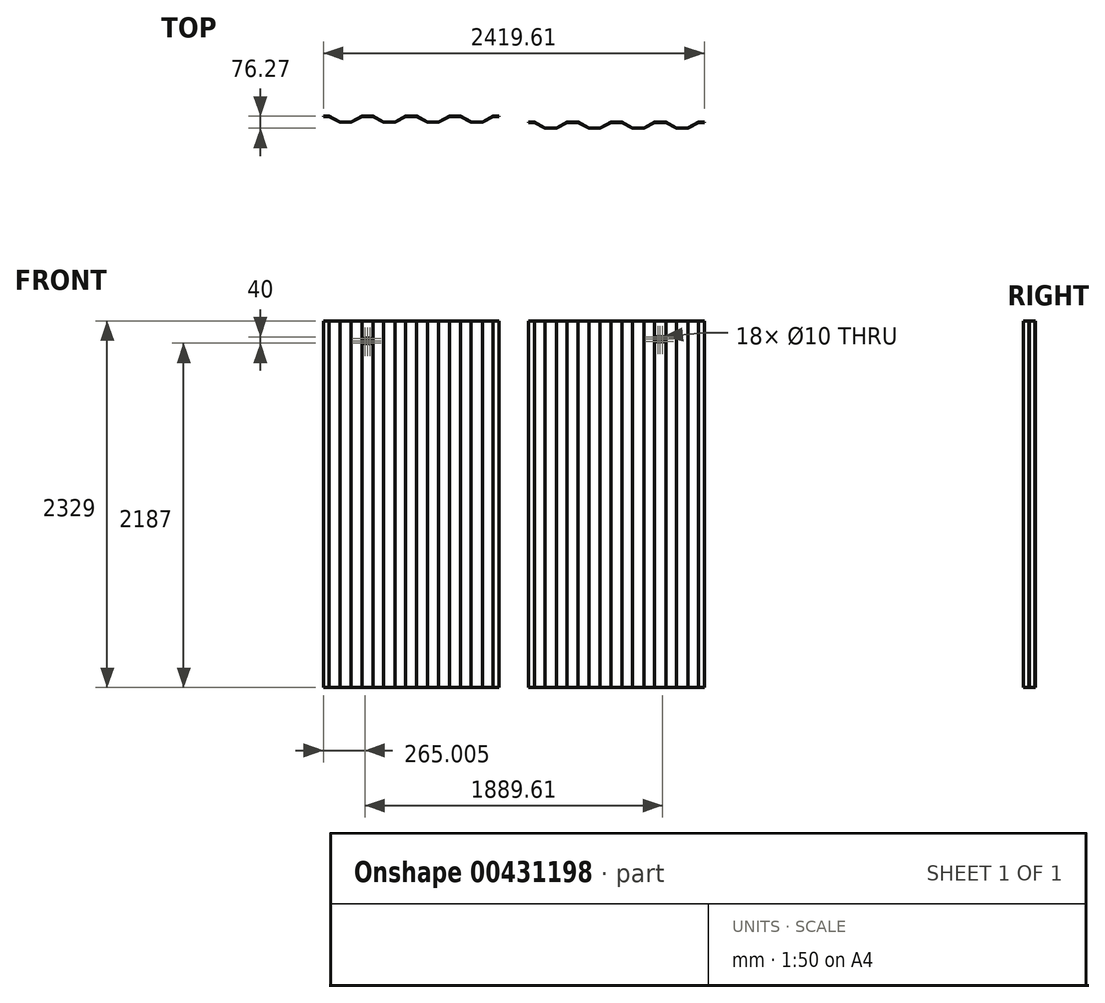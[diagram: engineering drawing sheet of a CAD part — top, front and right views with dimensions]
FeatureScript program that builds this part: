
annotation { "Feature Type Name" : "Feature", "Feature Type Description" : "" }
export const myFeature = defineFeature(function(context is Context, id is Id, definition is map)
    precondition{}
    {
        {
            var Q0;
            Q0=qCreatedBy(makeId("Top.planeOp"),FACE);
            var sketch = newSketch(context, id + "F0", { "sketchPlane" : qUnion([Q0])});
            skPoint(sketch, "E0", {"position": v(0, -36) * mm});
            skPoint(sketch, "E1", {"position": v(37, 0) * mm});
            skPoint(sketch, "E2", {"position": v(37, -36) * mm});
            skPoint(sketch, "E3", {"position": v(105, -36) * mm});
            skPoint(sketch, "E4", {"position": v(177, -36) * mm});
            skPoint(sketch, "E5", {"position": v(245, -36) * mm});
            skPoint(sketch, "E6", {"position": v(315, -36) * mm});
            skLineSegment(sketch, "E7", {"start": v(0, 0) * mm, "end": v(37, 0) * mm});
            skLineSegment(sketch, "E8", {"start": v(37, 0) * mm, "end": v(105, -36) * mm});
            skLineSegment(sketch, "E9", {"start": v(177, -36) * mm, "end": v(105, -36) * mm});
            skLineSegment(sketch, "E10", {"start": v(177, -36) * mm, "end": v(245, 0) * mm});
            skLineSegment(sketch, "E11", {"start": v(245, 0) * mm, "end": v(315, 0) * mm});
            skLineSegment(sketch, "E12.0", {"start": v(0, 2) * mm, "end": v(37.5, 2) * mm});
            skLineSegment(sketch, "E13", {"start": v(0, 0) * mm, "end": v(0, 2) * mm});
            skLineSegment(sketch, "E14.0", {"start": v(37.5, 2) * mm, "end": v(105.5, -34) * mm});
            skLineSegment(sketch, "E15.0", {"start": v(176.5, -34) * mm, "end": v(105.5, -34) * mm});
            skLineSegment(sketch, "E16.0", {"start": v(176.5, -34) * mm, "end": v(244.5, 2) * mm});
            skLineSegment(sketch, "E17.0", {"start": v(244.5, 2) * mm, "end": v(315.5, 2) * mm});
            skPoint(sketch, "E18", {"position": v(383, -36) * mm});
            skPoint(sketch, "E19", {"position": v(455, -36) * mm});
            skPoint(sketch, "E20", {"position": v(523, -36) * mm});
            skLineSegment(sketch, "E21", {"start": v(315, 0) * mm, "end": v(383, -36) * mm});
            skLineSegment(sketch, "E22", {"start": v(455, -36) * mm, "end": v(383, -36) * mm});
            skLineSegment(sketch, "E23", {"start": v(455, -36) * mm, "end": v(523, 0) * mm});
            skLineSegment(sketch, "E24", {"start": v(523, 0) * mm, "end": v(593, 0) * mm});
            skLineSegment(sketch, "E25.0", {"start": v(315.5, 2) * mm, "end": v(383.5, -34) * mm});
            skLineSegment(sketch, "E26.0", {"start": v(454.5, -34) * mm, "end": v(383.5, -34) * mm});
            skLineSegment(sketch, "E27.0", {"start": v(454.5, -34) * mm, "end": v(522.5, 2) * mm});
            skLineSegment(sketch, "E28.0", {"start": v(522.5, 2) * mm, "end": v(593.5, 2) * mm});
            skPoint(sketch, "E29", {"position": v(661, -36) * mm});
            skPoint(sketch, "E30", {"position": v(733, -36) * mm});
            skPoint(sketch, "E31", {"position": v(801, -36) * mm});
            skLineSegment(sketch, "E32", {"start": v(593, 0) * mm, "end": v(661, -36) * mm});
            skLineSegment(sketch, "E33", {"start": v(733, -36) * mm, "end": v(661, -36) * mm});
            skLineSegment(sketch, "E34", {"start": v(733, -36) * mm, "end": v(801, 0) * mm});
            skLineSegment(sketch, "E35", {"start": v(801, 0) * mm, "end": v(871, 0) * mm});
            skLineSegment(sketch, "E36.0", {"start": v(593.5, 2) * mm, "end": v(661.5, -34) * mm});
            skLineSegment(sketch, "E37.0", {"start": v(732.5, -34) * mm, "end": v(661.5, -34) * mm});
            skLineSegment(sketch, "E38.0", {"start": v(732.5, -34) * mm, "end": v(800.5, 2) * mm});
            skLineSegment(sketch, "E39.0", {"start": v(800.5, 2) * mm, "end": v(871.5, 2) * mm});
            skPoint(sketch, "E40", {"position": v(939, -36) * mm});
            skPoint(sketch, "E41", {"position": v(1011, -36) * mm});
            skPoint(sketch, "E42", {"position": v(1079, -36) * mm});
            skLineSegment(sketch, "E43", {"start": v(871, 0) * mm, "end": v(939, -36) * mm});
            skLineSegment(sketch, "E44", {"start": v(1011, -36) * mm, "end": v(939, -36) * mm});
            skLineSegment(sketch, "E45", {"start": v(1011, -36) * mm, "end": v(1079, 0) * mm});
            skLineSegment(sketch, "E46", {"start": v(1079, 0) * mm, "end": v(1116, 0) * mm});
            skLineSegment(sketch, "E47.0", {"start": v(871.5, 2) * mm, "end": v(939.5, -34) * mm});
            skLineSegment(sketch, "E48.0", {"start": v(1010.5, -34) * mm, "end": v(939.5, -34) * mm});
            skLineSegment(sketch, "E49.0", {"start": v(1010.5, -34) * mm, "end": v(1078.5, 2) * mm});
            skLineSegment(sketch, "E50", {"start": v(1078.5, 2) * mm, "end": v(1116, 2) * mm});
            skLineSegment(sketch, "E51", {"start": v(1116, 2) * mm, "end": v(1116, 0) * mm});
            skSolve(sketch);
        }
        {
            var Q0;
            Q0=qSketchRegion(id+"F0",true);
            extrude(context, id + "F1", {"entities" : qUnion([Q0]), "depth" : 2329 * mm});
        }
        {
            var Q0;
            Q0=makeQuery(id+"F1.opExtrude","SWEPT_FACE",FACE,{"disambiguationData":[OSD([sQuery(id+"F0.wireOp",EDGE,"E35")])]});
            var sketch = newSketch(context, id + "F2", { "sketchPlane" : qUnion([Q0])});
            skLineSegment(sketch, "E52", {"start": v(836, 2329) * mm, "end": v(836, 2227) * mm});
            skLineSegment(sketch, "E53", {"start": v(836, 2227) * mm, "end": v(821, 2227) * mm});
            skPoint(sketch, "E54", {"position": v(821, 2227) * mm});
            skPoint(sketch, "E55", {"position": v(836, 2227) * mm});
            skLineSegment(sketch, "E56", {"start": v(836, 2227) * mm, "end": v(851, 2227) * mm});
            skPoint(sketch, "E57", {"position": v(851, 2227) * mm});
            skLineSegment(sketch, "E58", {"start": v(836, 2227) * mm, "end": v(836, 2212) * mm});
            skLineSegment(sketch, "E59", {"start": v(836, 2212) * mm, "end": v(836, 2197) * mm});
            skPoint(sketch, "E60", {"position": v(821, 2212) * mm});
            skPoint(sketch, "E61", {"position": v(836, 2212) * mm});
            skPoint(sketch, "E62", {"position": v(851, 2212) * mm});
            skPoint(sketch, "E63", {"position": v(821, 2197) * mm});
            skPoint(sketch, "E64", {"position": v(836, 2197) * mm});
            skPoint(sketch, "E65", {"position": v(851, 2197) * mm});
            skSolve(sketch);
        }
        {
            var Q0;
            Q0=sQuery(id+"F2.wireOp",VERTEX,"E55");
            var Q1;
            Q1=sQuery(id+"F2.wireOp",VERTEX,"E57");
            var Q2;
            Q2=sQuery(id+"F2.wireOp",VERTEX,"E62");
            var Q3;
            Q3=sQuery(id+"F2.wireOp",VERTEX,"E61");
            var Q4;
            Q4=sQuery(id+"F2.wireOp",VERTEX,"E63");
            var Q5;
            Q5=sQuery(id+"F2.wireOp",VERTEX,"E64");
            var Q6;
            Q6=sQuery(id+"F2.wireOp",VERTEX,"E65");
            var Q7;
            Q7=sQuery(id+"F2.wireOp",VERTEX,"E60");
            var Q8;
            Q8=sQuery(id+"F2.wireOp",VERTEX,"E54");
            var Q9;
            Q9=makeQuery(id+"F1.opExtrude","SWEPT_BODY",BODY,{"disambiguationData":[OSD([sQuery(id+"F0.wireOp",EDGE,"E7"),sQuery(id+"F0.wireOp",EDGE,"E8"),sQuery(id+"F0.wireOp",EDGE,"E9"),sQuery(id+"F0.wireOp",EDGE,"E10"),sQuery(id+"F0.wireOp",EDGE,"E11"),sQuery(id+"F0.wireOp",EDGE,"E12.0"),sQuery(id+"F0.wireOp",EDGE,"E13"),sQuery(id+"F0.wireOp",EDGE,"E14.0"),sQuery(id+"F0.wireOp",EDGE,"E15.0"),sQuery(id+"F0.wireOp",EDGE,"E16.0"),sQuery(id+"F0.wireOp",EDGE,"E17.0"),sQuery(id+"F0.wireOp",EDGE,"E21"),sQuery(id+"F0.wireOp",EDGE,"E22"),sQuery(id+"F0.wireOp",EDGE,"E23"),sQuery(id+"F0.wireOp",EDGE,"E24"),sQuery(id+"F0.wireOp",EDGE,"E25.0"),sQuery(id+"F0.wireOp",EDGE,"E26.0"),sQuery(id+"F0.wireOp",EDGE,"E27.0"),sQuery(id+"F0.wireOp",EDGE,"E28.0"),sQuery(id+"F0.wireOp",EDGE,"E32"),sQuery(id+"F0.wireOp",EDGE,"E33"),sQuery(id+"F0.wireOp",EDGE,"E34"),sQuery(id+"F0.wireOp",EDGE,"E35"),sQuery(id+"F0.wireOp",EDGE,"E36.0"),sQuery(id+"F0.wireOp",EDGE,"E37.0"),sQuery(id+"F0.wireOp",EDGE,"E38.0"),sQuery(id+"F0.wireOp",EDGE,"E39.0"),sQuery(id+"F0.wireOp",EDGE,"E43"),sQuery(id+"F0.wireOp",EDGE,"E44"),sQuery(id+"F0.wireOp",EDGE,"E45"),sQuery(id+"F0.wireOp",EDGE,"E46"),sQuery(id+"F0.wireOp",EDGE,"E47.0"),sQuery(id+"F0.wireOp",EDGE,"E48.0"),sQuery(id+"F0.wireOp",EDGE,"E49.0"),sQuery(id+"F0.wireOp",EDGE,"E50"),sQuery(id+"F0.wireOp",EDGE,"E51")])]});
            hole(context, id + "F3", {"style" : HoleStyle.SIMPLE, "endStyle" : HoleEndStyle.THROUGH, "holeDiameter" : 10 * mm, "isTappedThrough" : true, "tappedDepth" : 12 * mm, "tapClearance" : 3, "locations" : qUnion([Q0, Q1, Q2, Q3, Q4, Q5, Q6, Q7, Q8]), "scope" : qUnion([Q9]), "startStyle" : HoleStartStyle.PART});
        }
        {
            var Q0;
            Q0=qCreatedBy(makeId("Top.planeOp"),FACE);
            var sketch = newSketch(context, id + "F4", { "sketchPlane" : qUnion([Q0])});
            skPoint(sketch, "E66", {"position": v(-1303.6, 2.27) * mm});
            skPoint(sketch, "E67", {"position": v(-1266.6, 38.27) * mm});
            skPoint(sketch, "E68", {"position": v(-1266.6, 2.27) * mm});
            skPoint(sketch, "E69", {"position": v(-1198.6, 2.27) * mm});
            skPoint(sketch, "E70", {"position": v(-1126.6, 2.27) * mm});
            skPoint(sketch, "E71", {"position": v(-1058.6, 2.27) * mm});
            skPoint(sketch, "E72", {"position": v(-988.6, 2.27) * mm});
            skLineSegment(sketch, "E73", {"start": v(-1303.6, 38.27) * mm, "end": v(-1266.6, 38.27) * mm});
            skLineSegment(sketch, "E74", {"start": v(-1266.6, 38.27) * mm, "end": v(-1198.6, 2.27) * mm});
            skLineSegment(sketch, "E75", {"start": v(-1126.6, 2.27) * mm, "end": v(-1198.6, 2.27) * mm});
            skLineSegment(sketch, "E76", {"start": v(-1126.6, 2.27) * mm, "end": v(-1058.6, 38.27) * mm});
            skLineSegment(sketch, "E77", {"start": v(-1058.6, 38.27) * mm, "end": v(-988.6, 38.27) * mm});
            skLineSegment(sketch, "E78.0", {"start": v(-1303.6, 40.27) * mm, "end": v(-1266.1, 40.27) * mm});
            skLineSegment(sketch, "E79", {"start": v(-1303.6, 38.27) * mm, "end": v(-1303.6, 40.27) * mm});
            skLineSegment(sketch, "E80.0", {"start": v(-1266.1, 40.27) * mm, "end": v(-1198.1, 4.27) * mm});
            skLineSegment(sketch, "E81.0", {"start": v(-1127.1, 4.27) * mm, "end": v(-1198.1, 4.27) * mm});
            skLineSegment(sketch, "E82.0", {"start": v(-1127.1, 4.27) * mm, "end": v(-1059.1, 40.27) * mm});
            skLineSegment(sketch, "E83.0", {"start": v(-1059.1, 40.27) * mm, "end": v(-988.1, 40.27) * mm});
            skPoint(sketch, "E84", {"position": v(-920.6, 2.27) * mm});
            skPoint(sketch, "E85", {"position": v(-848.6, 2.27) * mm});
            skPoint(sketch, "E86", {"position": v(-780.6, 2.27) * mm});
            skLineSegment(sketch, "E87", {"start": v(-988.6, 38.27) * mm, "end": v(-920.6, 2.27) * mm});
            skLineSegment(sketch, "E88", {"start": v(-848.6, 2.27) * mm, "end": v(-920.6, 2.27) * mm});
            skLineSegment(sketch, "E89", {"start": v(-848.6, 2.27) * mm, "end": v(-780.6, 38.27) * mm});
            skLineSegment(sketch, "E90", {"start": v(-780.6, 38.27) * mm, "end": v(-710.6, 38.27) * mm});
            skLineSegment(sketch, "E91.0", {"start": v(-988.1, 40.27) * mm, "end": v(-920.1, 4.27) * mm});
            skLineSegment(sketch, "E92.0", {"start": v(-849.1, 4.27) * mm, "end": v(-920.1, 4.27) * mm});
            skLineSegment(sketch, "E93.0", {"start": v(-849.1, 4.27) * mm, "end": v(-781.1, 40.27) * mm});
            skLineSegment(sketch, "E94.0", {"start": v(-781.1, 40.27) * mm, "end": v(-710.1, 40.27) * mm});
            skPoint(sketch, "E95", {"position": v(-642.6, 2.27) * mm});
            skPoint(sketch, "E96", {"position": v(-570.6, 2.27) * mm});
            skPoint(sketch, "E97", {"position": v(-502.6, 2.27) * mm});
            skLineSegment(sketch, "E98", {"start": v(-710.6, 38.27) * mm, "end": v(-642.6, 2.27) * mm});
            skLineSegment(sketch, "E99", {"start": v(-570.6, 2.27) * mm, "end": v(-642.6, 2.27) * mm});
            skLineSegment(sketch, "E100", {"start": v(-570.6, 2.27) * mm, "end": v(-502.6, 38.27) * mm});
            skLineSegment(sketch, "E101", {"start": v(-502.6, 38.27) * mm, "end": v(-432.6, 38.27) * mm});
            skLineSegment(sketch, "E102.0", {"start": v(-710.1, 40.27) * mm, "end": v(-642.1, 4.27) * mm});
            skLineSegment(sketch, "E103.0", {"start": v(-571.1, 4.27) * mm, "end": v(-642.1, 4.27) * mm});
            skLineSegment(sketch, "E104.0", {"start": v(-571.1, 4.27) * mm, "end": v(-503.1, 40.27) * mm});
            skLineSegment(sketch, "E105.0", {"start": v(-503.1, 40.27) * mm, "end": v(-432.1, 40.27) * mm});
            skPoint(sketch, "E106", {"position": v(-364.6, 2.27) * mm});
            skPoint(sketch, "E107", {"position": v(-292.6, 2.27) * mm});
            skPoint(sketch, "E108", {"position": v(-224.6, 2.27) * mm});
            skLineSegment(sketch, "E109", {"start": v(-432.6, 38.27) * mm, "end": v(-364.6, 2.27) * mm});
            skLineSegment(sketch, "E110", {"start": v(-292.6, 2.27) * mm, "end": v(-364.6, 2.27) * mm});
            skLineSegment(sketch, "E111", {"start": v(-292.6, 2.27) * mm, "end": v(-224.6, 38.27) * mm});
            skLineSegment(sketch, "E112", {"start": v(-224.6, 38.27) * mm, "end": v(-187.6, 38.27) * mm});
            skLineSegment(sketch, "E113.0", {"start": v(-432.1, 40.27) * mm, "end": v(-364.1, 4.27) * mm});
            skLineSegment(sketch, "E114.0", {"start": v(-293.1, 4.27) * mm, "end": v(-364.1, 4.27) * mm});
            skLineSegment(sketch, "E115.0", {"start": v(-293.1, 4.27) * mm, "end": v(-225.1, 40.27) * mm});
            skLineSegment(sketch, "E116", {"start": v(-225.1, 40.27) * mm, "end": v(-187.6, 40.27) * mm});
            skLineSegment(sketch, "E117", {"start": v(-187.6, 40.27) * mm, "end": v(-187.6, 38.27) * mm});
            skSolve(sketch);
        }
        {
            var Q0;
            Q0 = qSketchRegion(id + "F4", true);
            extrude(context, id + "F5", {"entities" : qUnion([Q0]), "depth" : 2329 * mm});
        }
        {
            var Q0;
            Q0=makeQuery(id+"F5.opExtrude","SWEPT_FACE",FACE,{"disambiguationData":[OSD([sQuery(id+"F4.wireOp",EDGE,"E77")])]});
            var sketch = newSketch(context, id + "F6", { "sketchPlane" : qUnion([Q0])});
            skLineSegment(sketch, "E118", {"start": v(-1023.6, 2329) * mm, "end": v(-1023.6, 2217) * mm});
            skLineSegment(sketch, "E119", {"start": v(-1023.6, 2217) * mm, "end": v(-1038.6, 2217) * mm});
            skLineSegment(sketch, "E120", {"start": v(-1023.6, 2217) * mm, "end": v(-1008.6, 2217) * mm});
            skLineSegment(sketch, "E121", {"start": v(-1023.6, 2217) * mm, "end": v(-1023.6, 2202) * mm});
            skLineSegment(sketch, "E122", {"start": v(-1023.6, 2202) * mm, "end": v(-1023.6, 2187) * mm});
            skLineSegment(sketch, "E123", {"start": v(-1023.6, 2187) * mm, "end": v(-1008.6, 2187) * mm});
            skLineSegment(sketch, "E124", {"start": v(-1038.6, 2217) * mm, "end": v(-1038.6, 2202) * mm});
            skLineSegment(sketch, "E125", {"start": v(-1038.6, 2202) * mm, "end": v(-1038.6, 2187) * mm});
            skLineSegment(sketch, "E126", {"start": v(-1008.6, 2217) * mm, "end": v(-1008.6, 2202) * mm});
            skLineSegment(sketch, "E127", {"start": v(-1008.6, 2202) * mm, "end": v(-1008.6, 2187) * mm});
            skSolve(sketch);
        }
        {
            var Q0;
            Q0=sQuery(id+"F6.wireOp",VERTEX,"E119.end");
            var Q1;
            Q1=sQuery(id+"F6.wireOp",VERTEX,"E119.start");
            var Q2;
            Q2=sQuery(id+"F6.wireOp",VERTEX,"E126.start");
            var Q3;
            Q3=sQuery(id+"F6.wireOp",VERTEX,"E126.end");
            var Q4;
            Q4=sQuery(id+"F6.wireOp",VERTEX,"E122.start");
            var Q5;
            Q5=sQuery(id+"F6.wireOp",VERTEX,"E125.start");
            var Q6;
            Q6=sQuery(id+"F6.wireOp",VERTEX,"E125.end");
            var Q7;
            Q7=sQuery(id+"F6.wireOp",VERTEX,"E123.start");
            var Q8;
            Q8=sQuery(id+"F6.wireOp",VERTEX,"E127.end");
            var Q9;
            Q9=makeQuery(id+"F5.opExtrude","SWEPT_BODY",BODY,{"disambiguationData":[OSD([sQuery(id+"F4.wireOp",EDGE,"E73"),sQuery(id+"F4.wireOp",EDGE,"E74"),sQuery(id+"F4.wireOp",EDGE,"E75"),sQuery(id+"F4.wireOp",EDGE,"E76"),sQuery(id+"F4.wireOp",EDGE,"E77"),sQuery(id+"F4.wireOp",EDGE,"E78.0"),sQuery(id+"F4.wireOp",EDGE,"E79"),sQuery(id+"F4.wireOp",EDGE,"E80.0"),sQuery(id+"F4.wireOp",EDGE,"E81.0"),sQuery(id+"F4.wireOp",EDGE,"E82.0"),sQuery(id+"F4.wireOp",EDGE,"E83.0"),sQuery(id+"F4.wireOp",EDGE,"E87"),sQuery(id+"F4.wireOp",EDGE,"E88"),sQuery(id+"F4.wireOp",EDGE,"E89"),sQuery(id+"F4.wireOp",EDGE,"E90"),sQuery(id+"F4.wireOp",EDGE,"E91.0"),sQuery(id+"F4.wireOp",EDGE,"E92.0"),sQuery(id+"F4.wireOp",EDGE,"E93.0"),sQuery(id+"F4.wireOp",EDGE,"E94.0"),sQuery(id+"F4.wireOp",EDGE,"E98"),sQuery(id+"F4.wireOp",EDGE,"E99"),sQuery(id+"F4.wireOp",EDGE,"E100"),sQuery(id+"F4.wireOp",EDGE,"E101"),sQuery(id+"F4.wireOp",EDGE,"E102.0"),sQuery(id+"F4.wireOp",EDGE,"E103.0"),sQuery(id+"F4.wireOp",EDGE,"E104.0"),sQuery(id+"F4.wireOp",EDGE,"E105.0"),sQuery(id+"F4.wireOp",EDGE,"E109"),sQuery(id+"F4.wireOp",EDGE,"E110"),sQuery(id+"F4.wireOp",EDGE,"E111"),sQuery(id+"F4.wireOp",EDGE,"E112"),sQuery(id+"F4.wireOp",EDGE,"E113.0"),sQuery(id+"F4.wireOp",EDGE,"E114.0"),sQuery(id+"F4.wireOp",EDGE,"E115.0"),sQuery(id+"F4.wireOp",EDGE,"E116"),sQuery(id+"F4.wireOp",EDGE,"E117")])]});
            hole(context, id + "F7", {"style" : HoleStyle.SIMPLE, "endStyle" : HoleEndStyle.THROUGH, "holeDiameter" : 10 * mm, "isTappedThrough" : true, "tappedDepth" : 12 * mm, "tapClearance" : 3, "locations" : qUnion([Q0, Q1, Q2, Q3, Q4, Q5, Q6, Q7, Q8]), "scope" : qUnion([Q9]), "startStyle" : HoleStartStyle.PART});
        }
    });
